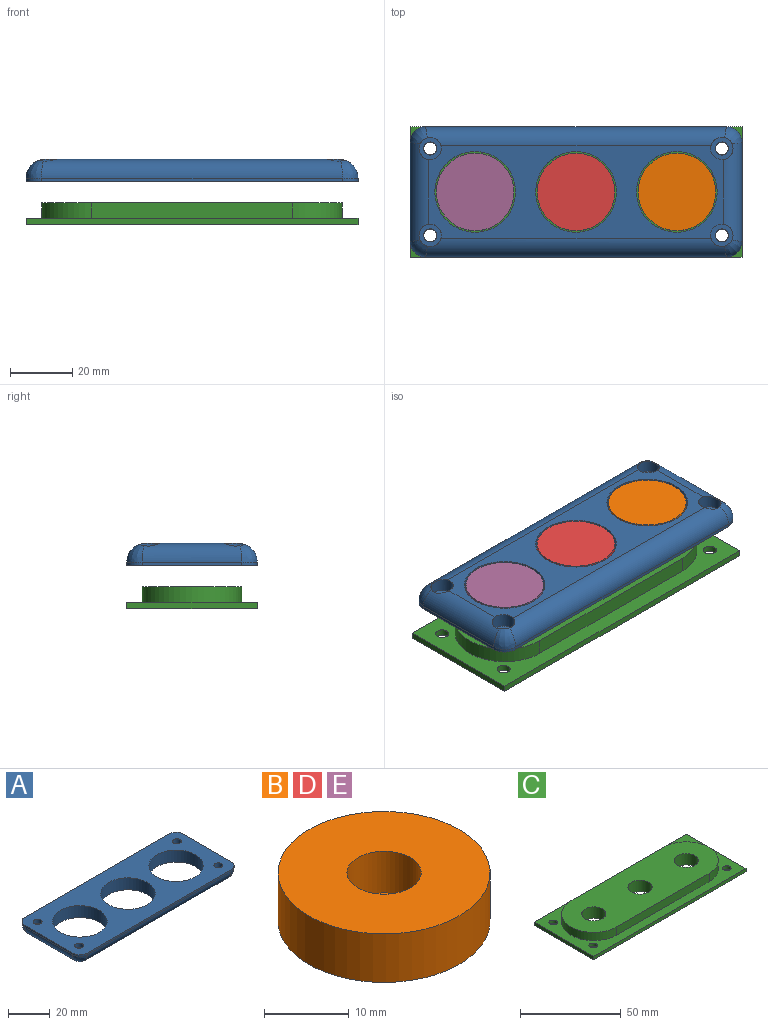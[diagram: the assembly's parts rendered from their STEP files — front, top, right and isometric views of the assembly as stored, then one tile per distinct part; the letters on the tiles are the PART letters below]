
ASSEMBLY  parts=5 mates=4
PART A: 33 faces, bbox 107x42x7 mm
  f0: plane 32x1mm, normal (-1,0,0), area 32mm2, adj f7,f21,f24,f25
  f1: plane 97x1mm, normal (0,-1,0), area 97mm2, adj f7,f21,f22,f28
  f2: plane 32x1mm, normal (1,0,0), area 32mm2, adj f7,f22,f23,f32
  f3: cylinder r=13mm len=26mm, axis (0,0,-1), area 571.8mm2, adj f7,f8
  f4: cylinder r=13mm len=26mm, axis (0,0,-1), area 571.8mm2, adj f7,f8
  f5: plane 97x1mm, normal (0,1,0), area 97mm2, adj f7,f23,f24,f29
  f6: cylinder r=13mm len=26mm, axis (0,0,-1), area 571.8mm2, adj f7,f8
  f7: plane 107x42mm, normal (0,0,1), area 2824.3mm2, adj f0,f1,f2,f3,f4,f5,f6,f17
  f8: plane 95x30mm, normal (0,0,-1), area 1193.1mm2, adj f3,f4,f6,f9,f11,f13,f15,f25
  f9: cylinder r=3.6mm len=7.2mm, axis (0,0,-1), area 94.9mm2, adj f8,f10,f25,f26,f28
  f10: plane 7.2x7.2mm, normal (0,0,-1), area 26.9mm2, adj f9,f20
  f11: cylinder r=3.6mm len=7.2mm, axis (0,0,-1), area 96mm2, adj f8,f12,f28,f30,f32
  f12: plane 7.2x7.2mm, normal (0,0,-1), area 26.9mm2, adj f11,f19
  f13: cylinder r=3.6mm len=7.2mm, axis (0,0,-1), area 96mm2, adj f8,f14,f29,f31,f32
  f14: plane 7.2x7.2mm, normal (0,0,-1), area 26.9mm2, adj f13,f18
  f15: cylinder r=3.6mm len=7.2mm, axis (0,0,-1), area 94.9mm2, adj f8,f16,f25,f27,f29
  f16: plane 7.2x7.2mm, normal (0,0,-1), area 26.9mm2, adj f15,f17
  f17: cylinder r=2.1mm len=4.2mm, axis (0,0,-1), area 33mm2, adj f7,f16
  f18: cylinder r=2.1mm len=4.2mm, axis (0,0,-1), area 33mm2, adj f7,f14
  f19: cylinder r=2.1mm len=4.2mm, axis (0,0,-1), area 33mm2, adj f7,f12
  f20: cylinder r=2.1mm len=4.2mm, axis (0,0,-1), area 33mm2, adj f7,f10
  f21: cylinder r=5mm len=5mm, axis (0,0,1), area 7.9mm2, adj f0,f1,f7,f26
  f22: cylinder r=5mm len=5mm, axis (0,0,-1), area 7.9mm2, adj f1,f2,f7,f30
  f23: cylinder r=5mm len=5mm, axis (0,0,1), area 7.9mm2, adj f2,f5,f7,f31
  f24: cylinder r=5mm len=5mm, axis (0,0,-1), area 7.9mm2, adj f0,f5,f7,f27
  f25: cylinder r=6mm len=32mm, axis (0,-1,0), area 268.6mm2, adj f0,f8,f9,f15,f26,f27
  f26: bspline ~6.29x5.65mm, area 44.2mm2, adj f9,f21,f25,f28
  f27: bspline ~6.29x5.65mm, area 44.2mm2, adj f15,f24,f25,f29
  f28: cylinder r=6mm len=97mm, axis (1,0,0), area 888.8mm2, adj f1,f8,f9,f11,f26,f30
  f29: cylinder r=6mm len=97mm, axis (-1,0,0), area 888.8mm2, adj f5,f8,f13,f15,f27,f31
  f30: bspline ~6.29x5.65mm, area 44.2mm2, adj f11,f22,f28,f32
  f31: bspline ~6.29x5.65mm, area 44.2mm2, adj f13,f23,f29,f32
  f32: cylinder r=6mm len=32mm, axis (0,1,0), area 268.4mm2, adj f2,f8,f11,f13,f30,f31
PART B: 5 faces, bbox 25x25x7 mm
  f0: cylinder r=12.5mm len=25mm, axis (0,0,-1), area 549.8mm2, adj f1,f2
  f1: plane 25x25mm, normal (0,0,1), area 430.7mm2, adj f0,f3
  f2: plane 25x25mm, normal (0,0,-1), area 490.9mm2, adj f0
  f3: cylinder r=4.38mm len=8.75mm, axis (0,0,1), area 164.9mm2, adj f1,f4
  f4: plane 8.75x8.75mm, normal (0,0,1), area 60.1mm2, adj f3
PART C: 18 faces, bbox 107x42x7 mm
  f0: plane 107x42mm, normal (0,0,1), area 1554.3mm2, adj f1,f2,f3,f6,f9,f10,f11,f12
  f1: plane 42x2mm, normal (-1,0,0), area 84mm2, adj f0,f2,f6,f8
  f2: plane 107x2mm, normal (0,-1,0), area 214mm2, adj f0,f1,f3,f8
  f3: plane 42x2mm, normal (1,0,0), area 84mm2, adj f0,f2,f6,f8
  f4: cylinder r=6mm len=12mm, axis (0,0,-1), area 263.9mm2, adj f8,f17
  f5: cylinder r=6mm len=12mm, axis (0,0,-1), area 263.9mm2, adj f8,f17
  f6: plane 107x2mm, normal (0,1,0), area 214mm2, adj f0,f1,f3,f8
  f7: cylinder r=6mm len=12mm, axis (0,0,-1), area 263.9mm2, adj f8,f17
  f8: plane 107x42mm, normal (0,0,-1), area 4099.3mm2, adj f1,f2,f3,f4,f5,f6,f7,f9
  f9: cylinder r=2.1mm len=4.2mm, axis (0,0,-1), area 26.4mm2, adj f0,f8
  f10: cylinder r=2.1mm len=4.2mm, axis (0,0,-1), area 26.4mm2, adj f0,f8
  f11: cylinder r=2.1mm len=4.2mm, axis (0,0,-1), area 26.4mm2, adj f0,f8
  f12: cylinder r=2.1mm len=4.2mm, axis (0,0,-1), area 26.4mm2, adj f0,f8
  f13: plane 65x5mm, normal (0,1,0), area 325mm2, adj f0,f14,f16,f17
  f14: cylinder r=16mm len=32mm, axis (0,0,-1), area 251.3mm2, adj f0,f13,f15,f17
  f15: plane 65x5mm, normal (0,-1,0), area 325mm2, adj f0,f14,f16,f17
  f16: cylinder r=16mm len=32mm, axis (0,0,-1), area 251.3mm2, adj f0,f13,f15,f17
  f17: plane 97x32mm, normal (0,0,1), area 2545mm2, adj f4,f5,f7,f13,f14,f15,f16
PART D: same geometry as B
PART E: same geometry as B
PLACE A rot(axis=(-1,0,0),180deg) t=(0,42,21)mm
PLACE B rot(axis=(-1,0,0),180deg) t=(86,21,21)mm
PLACE C at identity
PLACE D rot(axis=(-1,0,0),180deg) t=(53.5,21,21)mm
PLACE E rot(axis=(-1,0,0),180deg) t=(21,21,21)mm
MATE fastened E.f0 <-> A.f4  axis (0,0,1) through (21,21,21)mm
MATE fastened A.f3 <-> C.f4  axis (0,0,-1) through (53.5,21,14)mm
MATE fastened D.f0 <-> A.f3  axis (0,0,1) through (53.5,21,21)mm
MATE fastened B.f0 <-> A.f6  axis (0,0,1) through (86,21,21)mm
